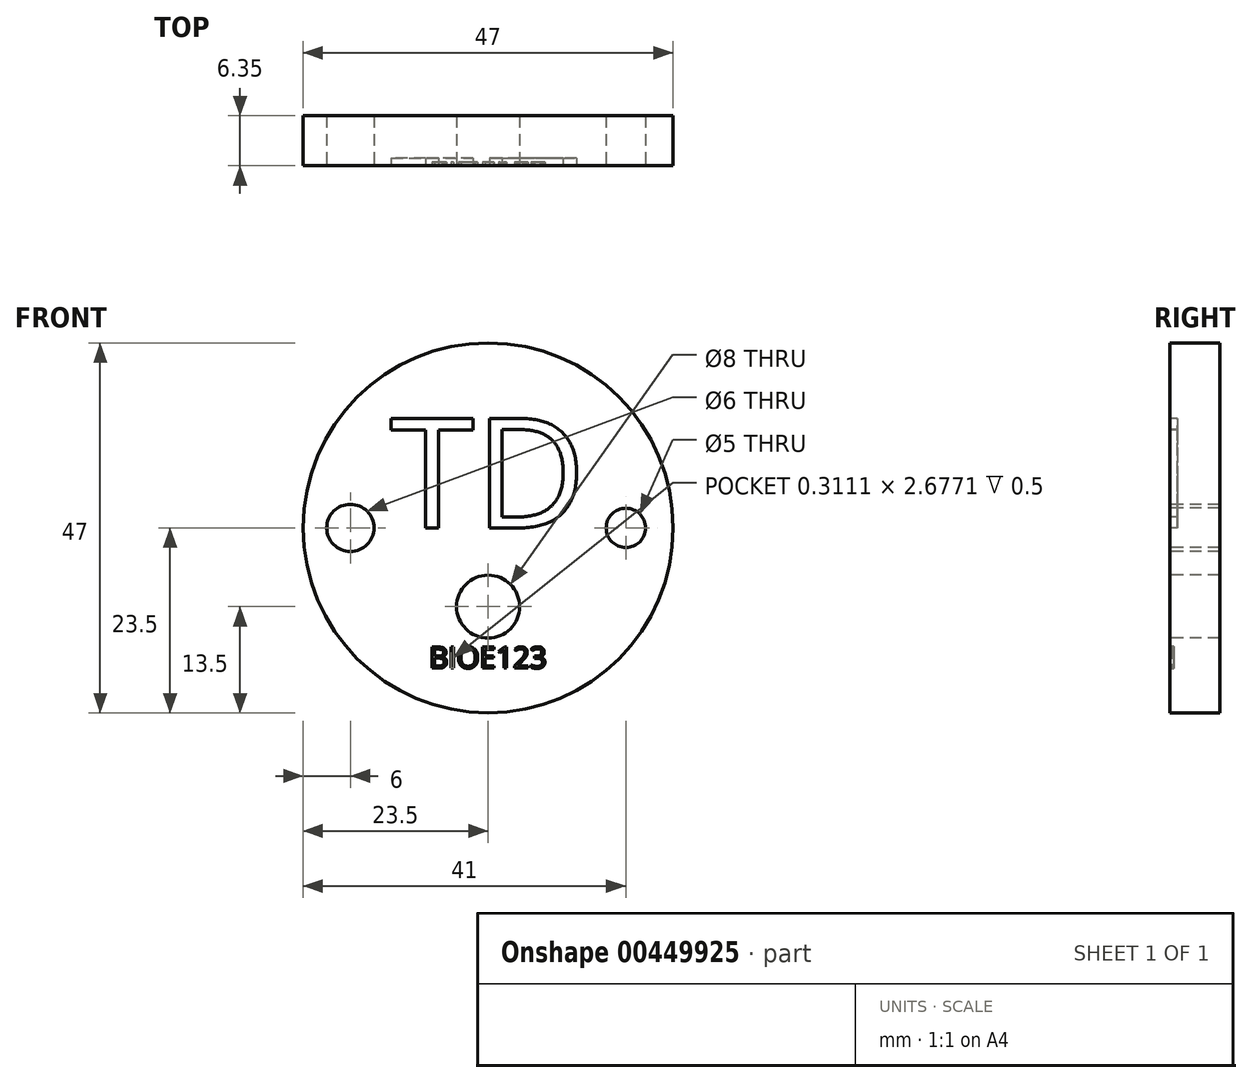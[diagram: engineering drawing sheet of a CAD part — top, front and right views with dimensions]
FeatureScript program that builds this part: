
annotation { "Feature Type Name" : "Feature", "Feature Type Description" : "" }
export const myFeature = defineFeature(function(context is Context, id is Id, definition is map)
    precondition{}
    {
        {
            var Q0;
            Q0=qCreatedBy(makeId("Front.planeOp"),FACE);
            var sketch = newSketch(context, id + "F0", { "sketchPlane" : qUnion([Q0])});
            skCircle(sketch, "E0", {"center": v(0, 0) * mm, "radius": 23.5 * mm});
            skSolve(sketch);
        }
        {
            var Q0;
            Q0 = qSketchRegion(id + "F0", true);
            extrude(context, id + "F1", {"entities" : qUnion([Q0]), "depth" : 6.35 * mm});
        }
        {
            var Q0;
            Q0=makeQuery(id+"F1.opExtrude","CAP_FACE",FACE,{"disambiguationData":[OSD([sQuery(id+"F0.wireOp",EDGE,"E0")])],"isStart":false});
            var sketch = newSketch(context, id + "F2", { "sketchPlane" : qUnion([Q0])});
            skCircle(sketch, "E1", {"center": v(17.5, 0) * mm, "radius": 2.5 * mm});
            skCircle(sketch, "E2", {"center": v(-17.5, 0) * mm, "radius": 3 * mm});
            skCircle(sketch, "E3", {"center": v(0, -10) * mm, "radius": 4 * mm});
            skSolve(sketch);
        }
        {
            var Q0;
            Q0 = qSketchRegion(id + "F2", true);
            extrude(context, id + "F3", {"entities" : qUnion([Q0]), "operationType" : NewBodyOperationType.REMOVE, "oppositeDirection" : true, "depth" : 6.35 * mm});
        }
        {
            var Q0;
            {var subQ0=sQuery(id+"F0.wireOp",EDGE,"E0");Q0=makeQuery(id+"F3.boolean.opBoolean","SPLIT",FACE,{"disambiguationData":[TD([makeQuery(id+"F1.opExtrude","SWEPT_FACE",FACE,{"disambiguationData":[OSD([subQ0])]})])],"derivedFrom":makeQuery(id+"F1.opExtrude","CAP_FACE",FACE,{"disambiguationData":[OSD([subQ0])],"isStart":false})});}
            var sketch = newSketch(context, id + "F4", { "sketchPlane" : qUnion([Q0])});
            skText(sketch, "E4", { "text": "BIOE123\n", "fontName": "OpenSans-Regular.ttf"});
            const initialGuessF4  = {"E4": [-0.00748, -0.01781, 1, 0, 0.0027]};
            skSetInitialGuess(sketch, initialGuessF4);
            skSolve(sketch);
        }
        {
            var Q0;
            Q0 = qSketchRegion(id + "F4", true);
            extrude(context, id + "F5", {"entities" : qUnion([Q0]), "operationType" : NewBodyOperationType.REMOVE, "oppositeDirection" : true, "depth" : 0.5 * mm});
        }
        {
            var Q0;
            {var subQ0=sQuery(id+"F0.wireOp",EDGE,"E0");Q0=makeQuery(id+"F5.boolean.opBoolean","SPLIT",FACE,{"disambiguationData":[TD([makeQuery(id+"F1.opExtrude","SWEPT_FACE",FACE,{"disambiguationData":[OSD([subQ0])]})])],"derivedFrom":makeQuery(id+"F1.opExtrude","CAP_FACE",FACE,{"disambiguationData":[OSD([subQ0])],"isStart":false})});}
            var sketch = newSketch(context, id + "F6", { "sketchPlane" : qUnion([Q0])});
            skText(sketch, "E5", { "text": "TD", "fontName": "OpenSans-Regular.ttf"});
            const initialGuessF6  = {"E5": [-0.0125, 0, 1, 0, 0.014]};
            skSetInitialGuess(sketch, initialGuessF6);
            skSolve(sketch);
        }
        {
            var Q0;
            Q0 = qSketchRegion(id + "F6", true);
            extrude(context, id + "F7", {"entities" : qUnion([Q0]), "operationType" : NewBodyOperationType.REMOVE, "oppositeDirection" : true, "depth" : 1 * mm});
        }
    });
